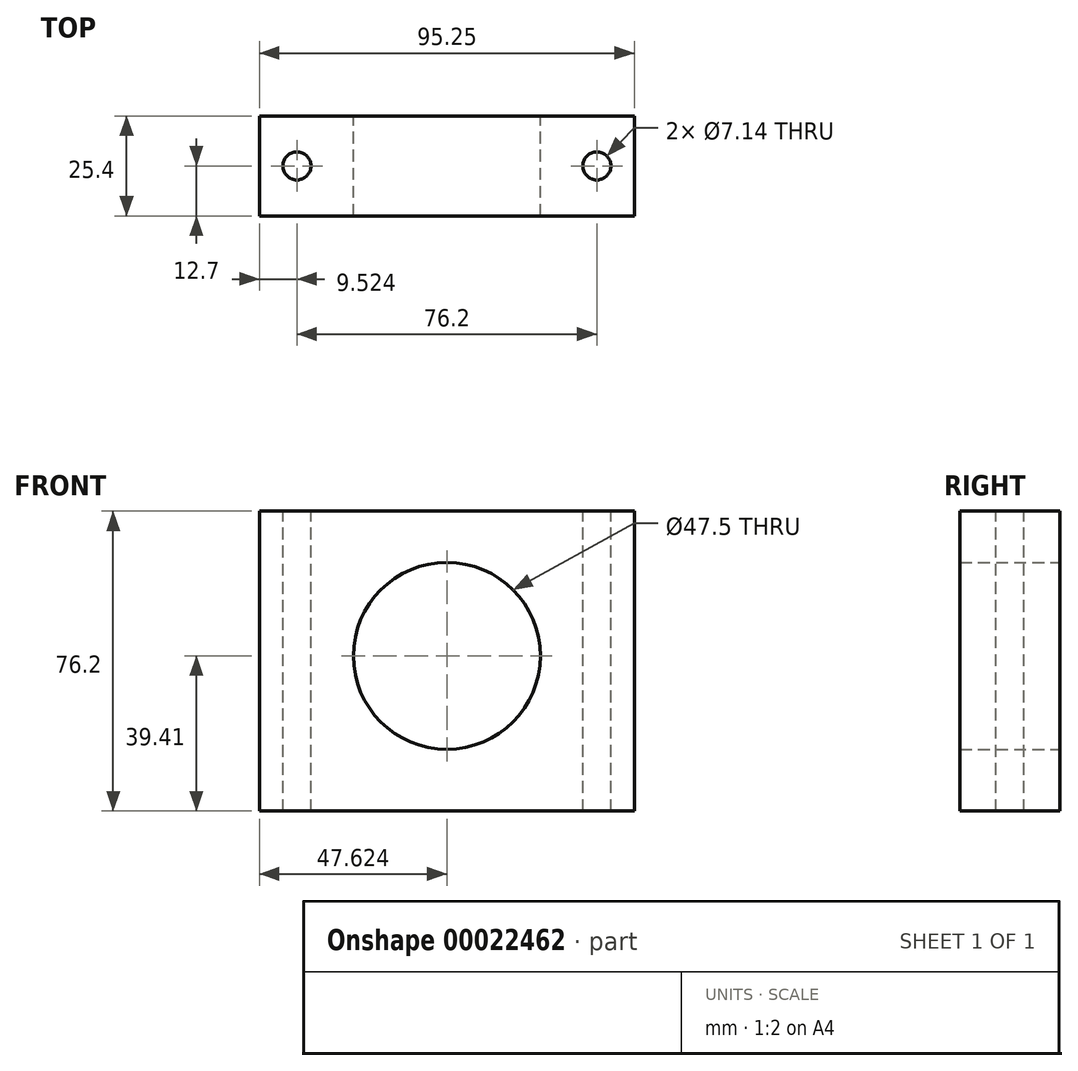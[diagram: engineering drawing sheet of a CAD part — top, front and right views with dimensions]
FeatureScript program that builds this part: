
annotation { "Feature Type Name" : "Feature", "Feature Type Description" : "" }
export const myFeature = defineFeature(function(context is Context, id is Id, definition is map)
    precondition{}
    {
        {
            var Q0;
            Q0=qCreatedBy(makeId("Front.planeOp"),FACE);
            var sketch = newSketch(context, id + "F0", { "sketchPlane" : qUnion([Q0])});
            skLineSegment(sketch, "E0.bottom", {"start": v(-71.24, 36.79) * mm, "end": v(24, 36.79) * mm});
            skLineSegment(sketch, "E0.top", {"start": v(-71.24, -39.41) * mm, "end": v(24, -39.41) * mm});
            skLineSegment(sketch, "E0.left", {"start": v(-71.24, 36.79) * mm, "end": v(-71.24, -39.41) * mm});
            skLineSegment(sketch, "E0.right", {"start": v(24, 36.79) * mm, "end": v(24, -39.41) * mm});
            skCircle(sketch, "E1", {"center": v(-23.62, 0) * mm, "radius": 23.75 * mm});
            skSolve(sketch);
        }
        {
            var Q0;
            Q0 = qSketchRegion(id + "F0", true);
            extrude(context, id + "F1", {"entities" : qUnion([Q0]), "depth" : 25.4 * mm});
        }
        {
            var Q0;
            Q0=makeQuery(id+"F1.opExtrude","SWEPT_FACE",FACE,{"disambiguationData":[OSD([sQuery(id+"F0.wireOp",EDGE,"E0.bottom")])]});
            var sketch = newSketch(context, id + "F2", { "sketchPlane" : qUnion([Q0])});
            skCircle(sketch, "E2", {"center": v(-61.72, -12.7) * mm, "radius": 3.57 * mm});
            skCircle(sketch, "E3", {"center": v(14.48, -12.7) * mm, "radius": 3.57 * mm});
            skSolve(sketch);
        }
        {
            var Q0;
            Q0=makeQuery(id+"F2.imprint","IMPRINT",FACE,{"disambiguationData":[TD([[makeQuery(id+"F2.imprint","IMPRINT",EDGE,{"derivedFrom":sQuery(id+"F2.wireOp",EDGE,"E2")}),1.0]])]});
            var Q1;
            Q1=makeQuery(id+"F2.imprint","IMPRINT",FACE,{"disambiguationData":[TD([[makeQuery(id+"F2.imprint","IMPRINT",EDGE,{"derivedFrom":sQuery(id+"F2.wireOp",EDGE,"E3")}),1.0]])]});
            extrude(context, id + "F3", {"entities" : qUnion([Q0, Q1]), "operationType" : NewBodyOperationType.REMOVE, "endBound" : BoundingType.THROUGH_ALL, "oppositeDirection" : true, "depth" : 25.4 * mm});
        }
    });
